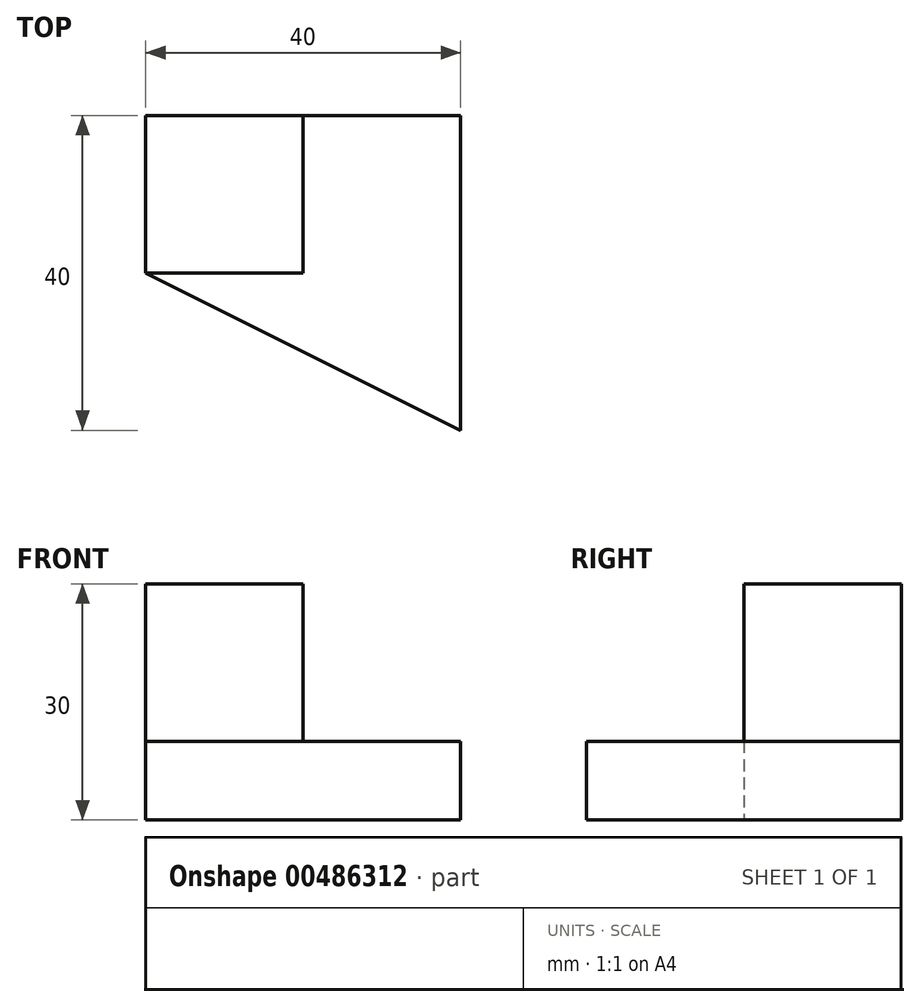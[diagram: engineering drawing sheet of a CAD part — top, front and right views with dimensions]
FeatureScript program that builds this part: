
annotation { "Feature Type Name" : "Feature", "Feature Type Description" : "" }
export const myFeature = defineFeature(function(context is Context, id is Id, definition is map)
    precondition{}
    {
        {
            var Q0;
            Q0=qCreatedBy(makeId("Top.planeOp"),FACE);
            var sketch = newSketch(context, id + "F0", { "sketchPlane" : qUnion([Q0])});
            skLineSegment(sketch, "E0.bottom", {"start": v(-48.66, 34.83) * mm, "end": v(-68.66, 34.83) * mm});
            skLineSegment(sketch, "E0.top", {"start": v(-48.66, 54.83) * mm, "end": v(-68.66, 54.83) * mm});
            skLineSegment(sketch, "E0.left", {"start": v(-48.66, 34.83) * mm, "end": v(-48.66, 54.83) * mm});
            skLineSegment(sketch, "E0.right", {"start": v(-68.66, 34.83) * mm, "end": v(-68.66, 54.83) * mm});
            skPoint(sketch, "E0.middle", {"position": v(-58.66, 44.83) * mm});
            skLineSegment(sketch, "E1", {"start": v(-48.66, 54.83) * mm, "end": v(-28.66, 54.83) * mm});
            skLineSegment(sketch, "E2", {"start": v(-28.66, 54.83) * mm, "end": v(-28.66, 14.83) * mm});
            skLineSegment(sketch, "E3", {"start": v(-68.66, 34.83) * mm, "end": v(-28.66, 14.83) * mm});
            skSolve(sketch);
        }
        {
            var Q0;
            Q0=makeQuery(id+"F0.imprint","IMPRINT",FACE,{"disambiguationData":[TD([[makeQuery(id+"F0.imprint","IMPRINT",EDGE,{"derivedFrom":sQuery(id+"F0.wireOp",EDGE,"E0.bottom")}),1.0]])]});
            extrude(context, id + "F1", {"entities" : qUnion([Q0]), "depth" : 10 * mm});
        }
        {
            var Q0;
            Q0=makeQuery(id+"F0.imprint","IMPRINT",FACE,{"disambiguationData":[TD([[makeQuery(id+"F0.imprint","IMPRINT",EDGE,{"derivedFrom":sQuery(id+"F0.wireOp",EDGE,"E0.bottom")}),-1.0]])]});
            extrude(context, id + "F2", {"entities" : qUnion([Q0]), "operationType" : NewBodyOperationType.ADD, "depth" : 30 * mm});
        }
    });
